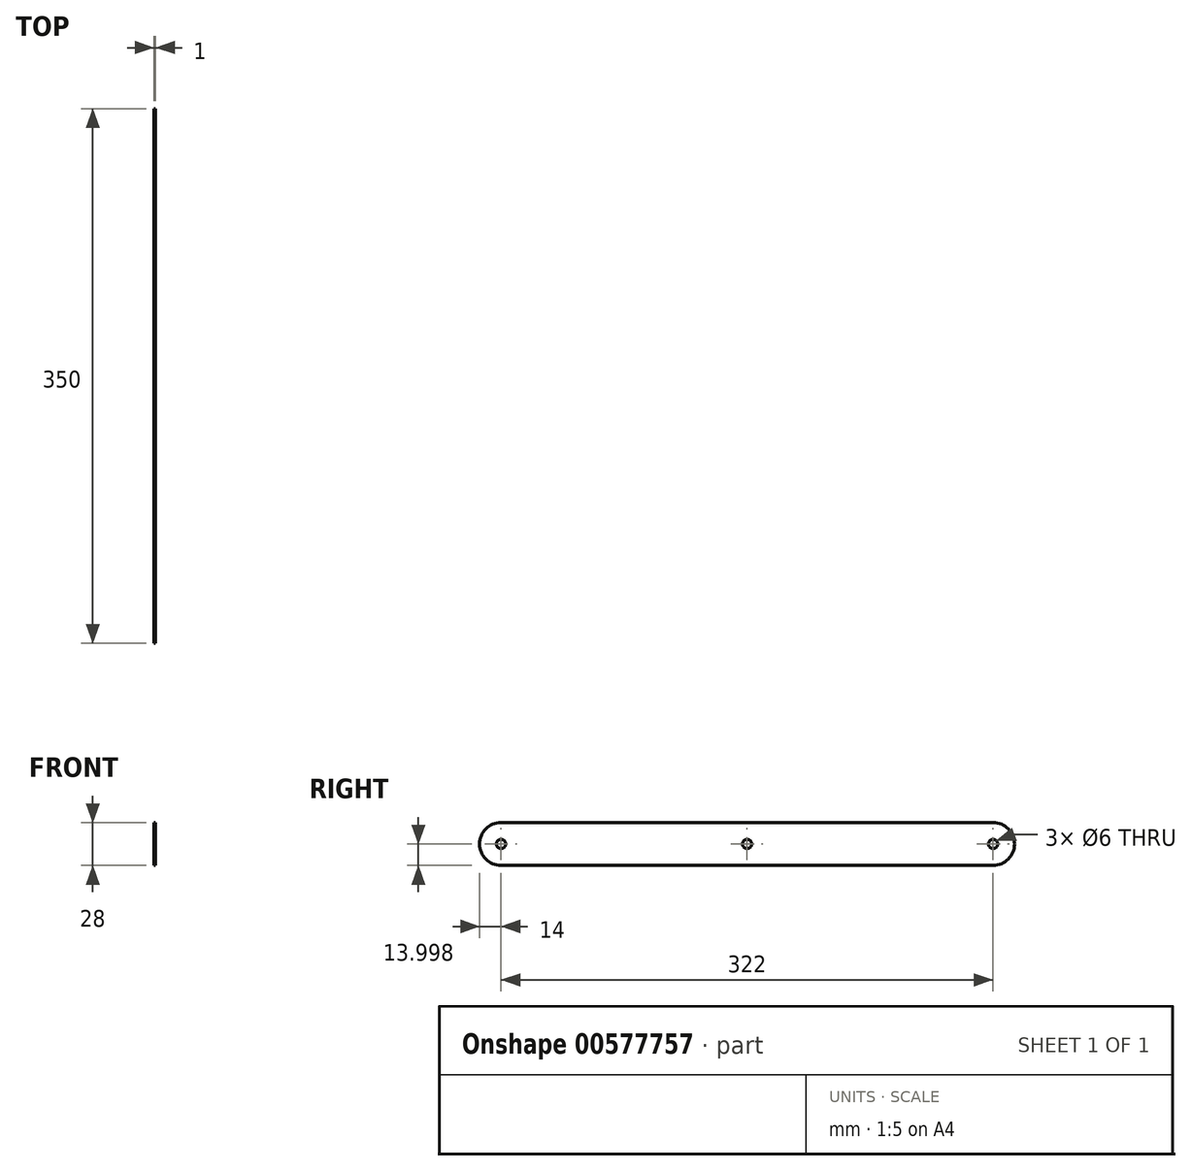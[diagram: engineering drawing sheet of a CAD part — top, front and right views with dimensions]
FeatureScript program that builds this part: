
annotation { "Feature Type Name" : "Feature", "Feature Type Description" : "" }
export const myFeature = defineFeature(function(context is Context, id is Id, definition is map)
    precondition{}
    {
        {
            var Q0;
            Q0=qCreatedBy(makeId("Right.planeOp"),FACE);
            var sketch = newSketch(context, id + "F0", { "sketchPlane" : qUnion([Q0])});
            skLineSegment(sketch, "E0.bottom", {"start": v(-166.76, 29.77) * mm, "end": v(183.24, 29.77) * mm});
            skLineSegment(sketch, "E0.top", {"start": v(-166.76, 1.77) * mm, "end": v(183.24, 1.77) * mm});
            skLineSegment(sketch, "E0.left", {"start": v(-166.76, 29.77) * mm, "end": v(-166.76, 1.77) * mm});
            skLineSegment(sketch, "E0.right", {"start": v(183.24, 29.77) * mm, "end": v(183.24, 1.77) * mm});
            skCircle(sketch, "E1", {"center": v(-152.76, 15.77) * mm, "radius": 14 * mm});
            skCircle(sketch, "E2", {"center": v(169.24, 15.77) * mm, "radius": 14 * mm});
            skCircle(sketch, "E3", {"center": v(-152.76, 15.77) * mm, "radius": 3 * mm});
            skCircle(sketch, "E4", {"center": v(169.24, 15.77) * mm, "radius": 3 * mm});
            skCircle(sketch, "E5", {"center": v(8.24, 15.77) * mm, "radius": 3 * mm});
            skSolve(sketch);
        }
        {
            var Q0;
            {var subQ0=sQuery(id+"F0.wireOp",EDGE,"E1");var subQ1=sQuery(id+"F0.wireOp",EDGE,"E0.bottom");var subQ2=makeQuery(id+"F0.imprint","INTERSECT",VERTEX,{"derivedFrom":[subQ1,subQ0]});Q0=makeQuery(id+"F0.imprint","IMPRINT",FACE,{"disambiguationData":[TD([[makeQuery(id+"F0.imprint","IMPRINT",EDGE,{"disambiguationData":[TD([[subQ2,-1.0]])],"derivedFrom":subQ1}),-1.0]])]});}
            var Q1;
            {var subQ0=sQuery(id+"F0.wireOp",EDGE,"E1");var subQ1=makeQuery(id+"F0.imprint","INTERSECT",VERTEX,{"derivedFrom":[sQuery(id+"F0.wireOp",EDGE,"E0.bottom"),subQ0]});Q1=makeQuery(id+"F0.imprint","IMPRINT",FACE,{"disambiguationData":[TD([[makeQuery(id+"F0.imprint","IMPRINT",EDGE,{"disambiguationData":[TD([[subQ1,-1.0]])],"derivedFrom":subQ0}),1.0]])]});}
            var Q2;
            {var subQ0=sQuery(id+"F0.wireOp",EDGE,"E2");var subQ1=makeQuery(id+"F0.imprint","INTERSECT",VERTEX,{"derivedFrom":[sQuery(id+"F0.wireOp",EDGE,"E0.bottom"),subQ0]});Q2=makeQuery(id+"F0.imprint","IMPRINT",FACE,{"disambiguationData":[TD([[makeQuery(id+"F0.imprint","IMPRINT",EDGE,{"disambiguationData":[TD([[subQ1,1.0]])],"derivedFrom":subQ0}),1.0]])]});}
            extrude(context, id + "F1", {"entities" : qUnion([Q0, Q1, Q2]), "depth" : 1 * mm, "offsetDistance" : 25 * mm});
        }
    });
